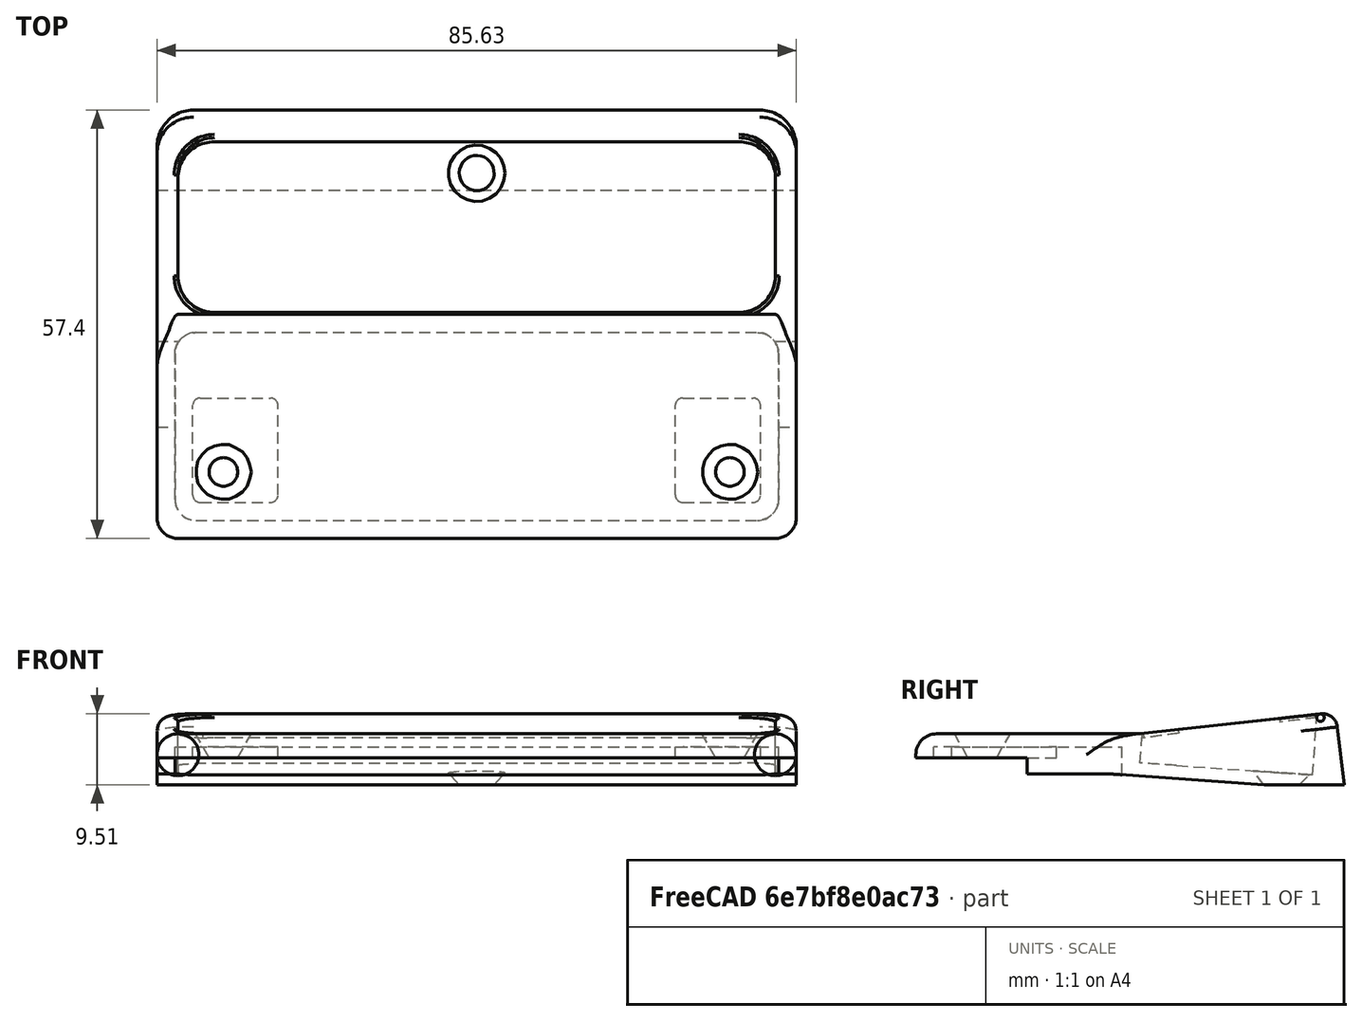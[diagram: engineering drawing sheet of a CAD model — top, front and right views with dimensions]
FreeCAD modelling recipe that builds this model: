
FCSTD DOCUMENT  (FreeCAD 0.14R3702 (Git))
Label: screen-door-handle-draft
License: CC-BY 3.0
LicenseURL: http://creativecommons.org/licenses/by/3.0/
objects: Part::Feature×10, PartDesign::Fillet×5, Part::Box×4, Part::MultiFuse×4, Part::Cone×3, Part::Cut×2, App::MeasureDistance×1, Part::Extrusion×1
note: 29 computed .brp shape members not serialized (recipe doc carries the construction recipe); baked Part::Feature solids carry a one-line shape summary decoded from their .brp

FEATURE [Part::Box] Box  label="bottom_pocket"
  Height = 10
  Length = 80.83
  Placement = pos=(2.4,2.4,-11.75) rot=(0,0,1;0rad)
  Width = 25.18
FEATURE [Part::Box] Box001  label="top_pocket"
  Height = 10
  Length = 80.03
  Placement = pos=(2.8,30.03,-3.9) rot=(-1,0,0;0.069813rad)
  Width = 23.17
FEATURE [Part::Cone] Cone  label="side_screw_pocket_002"
  Angle = 360
  Height = 3.5
  Placement = pos=(76.73,8.9,-3.4) rot=(0,0,1;0rad)
  Radius1 = 1.8
  Radius2 = 3.8
FEATURE [Part::Cone] Cone001  label="side_screw_pocket_001"
  Angle = 360
  Height = 3.5
  Placement = pos=(8.9,8.9,-3.4) rot=(0,0,1;0rad)
  Radius1 = 1.8
  Radius2 = 3.8
FEATURE [Part::Cone] Cone002  label="front_screw_pocket"
  Angle = 360
  Height = 1.8
  Placement = pos=(42.815,48.8,-7) rot=(-1,0,0;0.069813rad)
  Radius1 = 2.2
  Radius2 = 3.8
FEATURE [Part::Box] Box002  label="mounting_plate_001"
  Height = 2
  Length = 11.4
  Placement = pos=(4.8,4.8,-3.2) rot=(0,0,1;0rad)
  Width = 14
FEATURE [Part::Box] Box003  label="mounting_plate_002"
  Height = 2
  Length = 11.4
  Placement = pos=(69.43,4.8,-3.2) rot=(0,0,1;0rad)
  Width = 14
FEATURE [Part::Feature] Edge
  shape: bbox 2e-07 x 26.19 x 2.892 mm, 0 faces, 0 solids (baked)
FEATURE [Part::Feature] Edge001
  shape: bbox 2e-07 x 30 x 2e-07 mm, 0 faces, 0 solids (baked)
FEATURE [Part::Feature] Edge002
  shape: bbox 2e-07 x 2e-07 x 3.2 mm, 0 faces, 0 solids (baked)
FEATURE [Part::Feature] Edge003
  shape: bbox 2e-07 x 14.9 x 2e-07 mm, 0 faces, 0 solids (baked)
FEATURE [Part::Feature] Edge004
  shape: bbox 2e-07 x 2e-07 x 2.2 mm, 0 faces, 0 solids (baked)
FEATURE [Part::Feature] Edge005
  shape: bbox 2e-07 x 11.5 x 2e-07 mm, 0 faces, 0 solids (baked)
FEATURE [Part::Feature] Edge006
  shape: bbox 2e-07 x 20.23 x 1.415 mm, 0 faces, 0 solids (baked)
FEATURE [Part::Feature] Edge007
  shape: bbox 2e-07 x 10.77 x 2e-07 mm, 0 faces, 0 solids (baked)
FEATURE [Part::Feature] Edge008
  shape: bbox 2e-07 x 1.211 x 9.707 mm, 0 faces, 0 solids (baked)
FEATURE [App::MeasureDistance] Distance  label="Distance: 0.009"
  Distance = 0.00933526
  P1 = (0,9.25476,-3.2)
  P2 = (0,9.25233,-3.20901)
FEATURE [Part::Feature] Face
  shape: bbox 2e-07 x 57.41 x 9.714 mm, 1 faces, 0 solids (baked)
FEATURE [Part::Extrusion] Extrude  label="main_part_body"
  Base = -> Face
  Dir = (85.63,0,0)
  Solid = true
FEATURE [Part::MultiFuse] Fusion  label="pocketing"
  Shapes = -> [Cone002,Box001,Box]
FEATURE [Part::Cut] Cut  label="main_part_pocketed"
  Base = -> Extrude
  Tool = -> Fusion
FEATURE [Part::MultiFuse] Fusion001  label="mounting_plates"
  Shapes = -> [Box002,Box003]
FEATURE [Part::MultiFuse] Fusion002  label="side_screws"
  Shapes = -> [Cone001,Cone]
FEATURE [Part::MultiFuse] Fusion003  label="main_part_full"
  Shapes = -> [Cut,Fusion001]
FEATURE [Part::Cut] Cut001  label="handle_main"
  Base = -> Fusion003
  Tool = -> Fusion002
FEATURE [PartDesign::Fillet] Fillet
  Base = -> Cut001 [Edge56,Edge55,Edge60,Edge58,Edge11,Edge18]
  Radius = 4.88
FEATURE [PartDesign::Fillet] Fillet001
  Base = -> Fillet [Edge3,Edge25,Edge5,Edge80,Edge82,Edge83,Edge85,Edge37,Edge26]
  Radius = 2.8
FEATURE [PartDesign::Fillet] Fillet002
  Base = -> Fillet001 [Edge35,Edge34,Edge37]
  Radius = 2
FEATURE [PartDesign::Fillet] Fillet003
  Base = -> Fillet002 [Edge155,Edge156,Edge147,Edge148,Edge160,Edge158,Edge152,Edge150]
  Radius = 1
FEATURE [PartDesign::Fillet] Fillet004  label="handle_final"
  Base = -> Fillet003 [Edge173]
  Radius = 0.5
